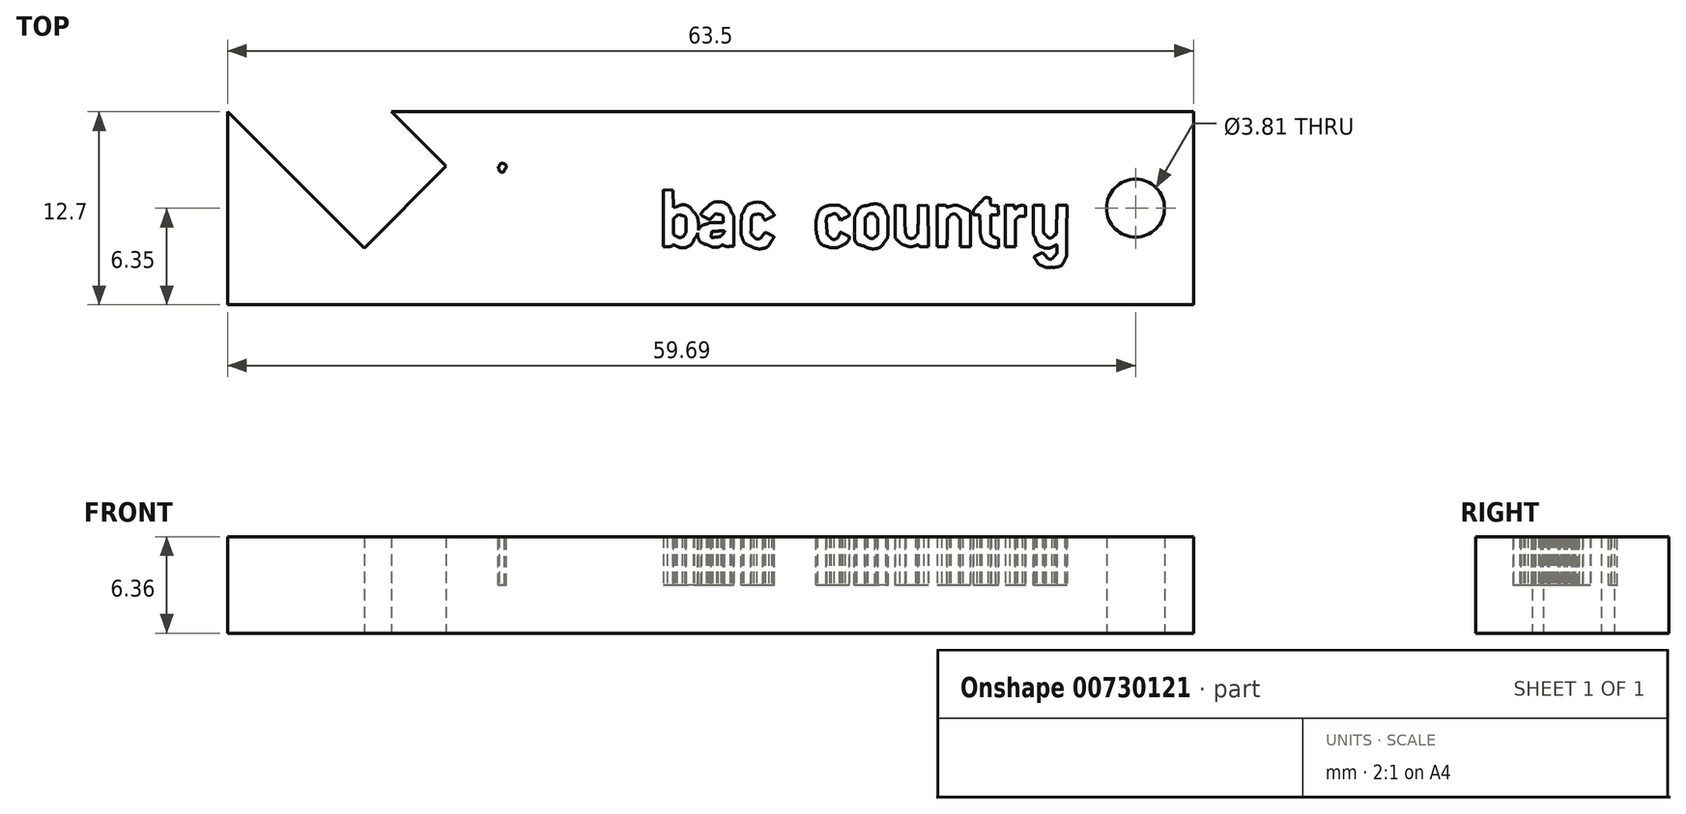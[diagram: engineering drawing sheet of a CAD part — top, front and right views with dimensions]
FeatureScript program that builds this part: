
annotation { "Feature Type Name" : "Feature", "Feature Type Description" : "" }
export const myFeature = defineFeature(function(context is Context, id is Id, definition is map)
    precondition{}
    {
        {
            var Q0;
            Q0=qCreatedBy(makeId("Top.planeOp"),FACE);
            var sketch = newSketch(context, id + "F0", { "sketchPlane" : qUnion([Q0])});
            skLineSegment(sketch, "E0.bottom", {"start": v(31.75, -6.35) * mm, "end": v(-31.75, -6.35) * mm});
            skLineSegment(sketch, "E0.top", {"start": v(31.75, 6.35) * mm, "end": v(-31.75, 6.35) * mm, "construction": true});
            skLineSegment(sketch, "E0.left", {"start": v(31.75, -6.35) * mm, "end": v(31.75, 6.35) * mm});
            skLineSegment(sketch, "E0.right", {"start": v(-31.75, -6.35) * mm, "end": v(-31.75, 6.35) * mm});
            skPoint(sketch, "E0.middle", {"position": v(0, 0) * mm});
            skLineSegment(sketch, "E1", {"start": v(-20.97, 6.35) * mm, "end": v(31.75, 6.35) * mm});
            skLineSegment(sketch, "E2", {"start": v(31.75, 0) * mm, "end": v(27.94, 0) * mm, "construction": true});
            skCircle(sketch, "E3", {"center": v(27.94, 0) * mm, "radius": 1.9 * mm});
            skLineSegment(sketch, "E4", {"start": v(-22.77, -2.63) * mm, "end": v(-17.38, 2.76) * mm});
            skLineSegment(sketch, "E5", {"start": v(-31.75, 6.35) * mm, "end": v(-22.77, -2.63) * mm});
            skLineSegment(sketch, "E6", {"start": v(-20.97, 6.35) * mm, "end": v(-17.38, 2.76) * mm});
            skSolve(sketch);
        }
        {
            var Q0;
            Q0 = qSketchRegion(id + "F0", true);
            extrude(context, id + "F1", {"entities" : qUnion([Q0]), "endBound" : BoundingType.SYMMETRIC, "depth" : 6.35 * mm, "offsetDistance" : 25.4 * mm});
        }
        {
            var Q0;
            Q0=qCreatedBy(makeId("Top.planeOp"),FACE);
            var sketch = newSketch(context, id + "F2", { "sketchPlane" : qUnion([Q0])});
            skFitSpline(sketch, "E7", {"points": [v(-7.2, -5.12) * mm, v(-7.28, -5.08) * mm, v(-7.3, -5) * mm, v(-7.3, -4.6) * mm]});
            skFitSpline(sketch, "E8", {"points": [v(-7.3, -4.6) * mm, v(-7.3, -3.8) * mm, v(-7.5, -3.27) * mm, v(-8, -2.72) * mm]});
            skFitSpline(sketch, "E9", {"points": [v(-8, -2.72) * mm, v(-8.19, -2.52) * mm, v(-8.4, -2.36) * mm, v(-8.62, -2.25) * mm]});
            skFitSpline(sketch, "E10", {"points": [v(-8.62, -2.25) * mm, v(-8.95, -2.1) * mm, v(-8.98, -2.09) * mm, v(-9.6, -2.09) * mm]});
            skFitSpline(sketch, "E11", {"points": [v(-9.6, -2.09) * mm, v(-10.36, -2.09) * mm, v(-10.68, -2.17) * mm, v(-11.16, -2.5) * mm]});
            skFitSpline(sketch, "E12", {"points": [v(-11.16, -2.5) * mm, v(-11.76, -2.9) * mm, v(-12.2, -3.6) * mm, v(-12.44, -4.56) * mm]});
            skFitSpline(sketch, "E13", {"points": [v(-12.97, -5.08) * mm, v(-13.54, -5.08) * mm, v(-13.53, -5.1) * mm, v(-13.39, -4.14) * mm]});
            skFitSpline(sketch, "E14", {"points": [v(-13.39, -4.14) * mm, v(-13.32, -3.71) * mm, v(-13.25, -3.16) * mm, v(-13.23, -2.9) * mm]});
            skLineSegment(sketch, "E15", {"start": v(-12.44, -4.56) * mm, "end": v(-12.58, -5.08) * mm});
            skLineSegment(sketch, "E16", {"start": v(-12.58, -5.08) * mm, "end": v(-12.97, -5.08) * mm});
            skFitSpline(sketch, "E17", {"points": [v(-13.43, -2.09) * mm, v(-13.73, -1.63) * mm, v(-13.83, -1.24) * mm, v(-13.74, -0.83) * mm]});
            skFitSpline(sketch, "E18", {"points": [v(-13.74, -0.83) * mm, v(-13.71, -0.68) * mm, v(-13.56, -0.26) * mm, v(-13.4, 0.1) * mm]});
            skFitSpline(sketch, "E19", {"points": [v(-13.4, 0.1) * mm, v(-13.1, 0.85) * mm, v(-13.05, 1.1) * mm, v(-13.24, 1.23) * mm]});
            skFitSpline(sketch, "E20", {"points": [v(-13.24, 1.23) * mm, v(-13.4, 1.34) * mm, v(-13.55, 1.33) * mm, v(-13.7, 1.22) * mm]});
            skFitSpline(sketch, "E21", {"points": [v(-13.7, 1.22) * mm, v(-13.8, 1.13) * mm, v(-13.82, 1.07) * mm, v(-13.82, 0.8) * mm]});
            skFitSpline(sketch, "E22", {"points": [v(-13.82, 0.8) * mm, v(-13.83, 0.62) * mm, v(-13.83, 0.43) * mm, v(-13.84, 0.38) * mm]});
            skFitSpline(sketch, "E23", {"points": [v(-13.84, 0.38) * mm, v(-13.84, 0.28) * mm, v(-14.07, 0) * mm, v(-14.2, -0.07) * mm]});
            skFitSpline(sketch, "E24", {"points": [v(-14.2, -0.07) * mm, v(-14.3, -0.12) * mm, v(-14.3, -0.12) * mm, v(-14.25, -0.01) * mm]});
            skFitSpline(sketch, "E25", {"points": [v(-14.25, -0.01) * mm, v(-14.15, 0.17) * mm, v(-14.18, 0.5) * mm, v(-14.32, 0.8) * mm]});
            skFitSpline(sketch, "E26", {"points": [v(-14.32, 0.8) * mm, v(-14.4, 0.96) * mm, v(-14.45, 1.14) * mm, v(-14.45, 1.2) * mm]});
            skFitSpline(sketch, "E27", {"points": [v(-14.45, 1.2) * mm, v(-14.46, 1.28) * mm, v(-14.52, 1.38) * mm, v(-14.61, 1.46) * mm]});
            skLineSegment(sketch, "E28", {"start": v(-13.23, -2.9) * mm, "end": v(-13.18, -2.45) * mm});
            skLineSegment(sketch, "E29", {"start": v(-13.18, -2.45) * mm, "end": v(-13.43, -2.09) * mm});
            skFitSpline(sketch, "E30", {"points": [v(-14.69, 1.8) * mm, v(-14.64, 1.91) * mm, v(-14.53, 2.27) * mm, v(-14.45, 2.6) * mm]});
            skFitSpline(sketch, "E31", {"points": [v(-14.45, 2.6) * mm, v(-14.26, 3.33) * mm, v(-14.17, 3.5) * mm, v(-13.8, 3.92) * mm]});
            skFitSpline(sketch, "E32", {"points": [v(-13.8, 3.92) * mm, v(-13.08, 4.73) * mm, v(-12.06, 5.1) * mm, v(-10.83, 5.02) * mm]});
            skFitSpline(sketch, "E33", {"points": [v(-10.83, 5.02) * mm, v(-10.16, 4.98) * mm, v(-9.61, 4.83) * mm, v(-9.01, 4.54) * mm]});
            skFitSpline(sketch, "E34", {"points": [v(-9.01, 4.54) * mm, v(-8.14, 4.1) * mm, v(-7.55, 3.53) * mm, v(-7.15, 2.72) * mm]});
            skFitSpline(sketch, "E35", {"points": [v(-7.15, 2.72) * mm, v(-6.84, 2.1) * mm, v(-6.84, 2) * mm, v(-7.13, 2.36) * mm]});
            skFitSpline(sketch, "E36", {"points": [v(-7.13, 2.36) * mm, v(-7.64, 2.97) * mm, v(-8.27, 3.48) * mm, v(-8.85, 3.74) * mm]});
            skFitSpline(sketch, "E37", {"points": [v(-8.85, 3.74) * mm, v(-9.16, 3.89) * mm, v(-9.86, 4.08) * mm, v(-10.05, 4.07) * mm]});
            skFitSpline(sketch, "E38", {"points": [v(-10.05, 4.07) * mm, v(-10.19, 4.06) * mm, v(-10.18, 4.06) * mm, v(-10.03, 4.01) * mm]});
            skFitSpline(sketch, "E39", {"points": [v(-10.03, 4.01) * mm, v(-8.6, 3.5) * mm, v(-7.65, 2.63) * mm, v(-7.13, 1.31) * mm]});
            skLineSegment(sketch, "E40", {"start": v(-14.61, 1.46) * mm, "end": v(-14.77, 1.6) * mm});
            skLineSegment(sketch, "E41", {"start": v(-14.77, 1.6) * mm, "end": v(-14.69, 1.8) * mm});
            skFitSpline(sketch, "E42", {"points": [v(-7.13, 1.16) * mm, v(-7.62, 1.8) * mm, v(-8.3, 2.37) * mm, v(-8.9, 2.68) * mm]});
            skFitSpline(sketch, "E43", {"points": [v(-8.9, 2.68) * mm, v(-9.76, 3.12) * mm, v(-10.69, 3.14) * mm, v(-11.12, 2.73) * mm]});
            skFitSpline(sketch, "E44", {"points": [v(-11.12, 2.73) * mm, v(-11.63, 2.26) * mm, v(-11.4, 1.47) * mm, v(-10.65, 1.13) * mm]});
            skFitSpline(sketch, "E45", {"points": [v(-10.65, 1.13) * mm, v(-10.24, 0.94) * mm, v(-9.84, 0.86) * mm, v(-8.91, 0.78) * mm]});
            skFitSpline(sketch, "E46", {"points": [v(-8.91, 0.78) * mm, v(-7.92, 0.69) * mm, v(-7.74, 0.65) * mm, v(-7.34, 0.44) * mm]});
            skFitSpline(sketch, "E47", {"points": [v(-7.34, 0.44) * mm, v(-6.83, 0.17) * mm, v(-6.44, -0.3) * mm, v(-6.32, -0.75) * mm]});
            skFitSpline(sketch, "E48", {"points": [v(-6.32, -0.75) * mm, v(-6.25, -1.03) * mm, v(-6.33, -1.46) * mm, v(-6.52, -1.83) * mm]});
            skFitSpline(sketch, "E49", {"points": [v(-6.52, -1.83) * mm, v(-6.76, -2.3) * mm, v(-6.76, -2.56) * mm, v(-6.54, -2.98) * mm]});
            skFitSpline(sketch, "E50", {"points": [v(-6.54, -2.98) * mm, v(-6.46, -3.12) * mm, v(-6.44, -3.32) * mm, v(-6.41, -3.8) * mm]});
            skFitSpline(sketch, "E51", {"points": [v(-6.41, -3.8) * mm, v(-6.4, -4.18) * mm, v(-6.35, -4.56) * mm, v(-6.3, -4.73) * mm]});
            skFitSpline(sketch, "E52", {"points": [v(-6.3, -4.73) * mm, v(-6.18, -5.13) * mm, v(-6.22, -5.18) * mm, v(-6.73, -5.18) * mm]});
            skFitSpline(sketch, "E53", {"points": [v(-6.73, -5.18) * mm, v(-6.94, -5.18) * mm, v(-7.16, -5.15) * mm, v(-7.2, -5.12) * mm]});
            skLineSegment(sketch, "E54", {"start": v(-7.13, 1.31) * mm, "end": v(-7, 0.98) * mm});
            skLineSegment(sketch, "E55", {"start": v(-7, 0.98) * mm, "end": v(-7.13, 1.16) * mm});
            skFitSpline(sketch, "E56", {"points": [v(-13.54, 2.54) * mm, v(-13.41, 2.77) * mm, v(-13.73, 2.97) * mm, v(-13.9, 2.77) * mm]});
            skFitSpline(sketch, "E57", {"points": [v(-13.9, 2.77) * mm, v(-13.94, 2.7) * mm, v(-13.95, 2.66) * mm, v(-13.9, 2.56) * mm]});
            skFitSpline(sketch, "E58", {"points": [v(-13.9, 2.56) * mm, v(-13.83, 2.4) * mm, v(-13.61, 2.4) * mm, v(-13.54, 2.54) * mm]});
            skFitSpline(sketch, "E59", {"points": [v(22, -3.87) * mm, v(21.68, -3.74) * mm, v(21.56, -3.65) * mm, v(21.42, -3.46) * mm]});
            skFitSpline(sketch, "E60", {"points": [v(21.42, -3.46) * mm, v(21.34, -3.34) * mm, v(21.28, -3.22) * mm, v(21.3, -3.2) * mm]});
            skFitSpline(sketch, "E61", {"points": [v(21.3, -3.2) * mm, v(21.3, -3.17) * mm, v(21.44, -3.1) * mm, v(21.58, -3.04) * mm]});
            skLineSegment(sketch, "E62", {"start": v(-13.54, 2.54) * mm, "end": v(-13.54, 2.54) * mm});
            skFitSpline(sketch, "E63", {"points": [v(22, -3.1) * mm, v(22.23, -3.33) * mm, v(22.4, -3.35) * mm, v(22.6, -3.14) * mm]});
            skFitSpline(sketch, "E64", {"points": [v(22.6, -3.14) * mm, v(22.74, -3) * mm, v(22.76, -2.95) * mm, v(22.76, -2.7) * mm]});
            skFitSpline(sketch, "E65", {"points": [v(22.76, -2.7) * mm, v(22.76, -2.44) * mm, v(22.75, -2.41) * mm, v(22.67, -2.44) * mm]});
            skFitSpline(sketch, "E66", {"points": [v(22.67, -2.44) * mm, v(22.2, -2.64) * mm, v(21.57, -2.4) * mm, v(21.34, -1.96) * mm]});
            skFitSpline(sketch, "E67", {"points": [v(21.34, -1.96) * mm, v(21.23, -1.75) * mm, v(21.22, -1.67) * mm, v(21.22, -0.77) * mm]});
            skLineSegment(sketch, "E68", {"start": v(21.58, -3.04) * mm, "end": v(21.83, -2.92) * mm});
            skLineSegment(sketch, "E69", {"start": v(21.83, -2.92) * mm, "end": v(22, -3.1) * mm});
            skFitSpline(sketch, "E70", {"points": [v(22.04, -1.76) * mm, v(22.22, -1.94) * mm, v(22.4, -1.95) * mm, v(22.59, -1.78) * mm]});
            skLineSegment(sketch, "E71", {"start": v(21.22, -0.77) * mm, "end": v(21.22, 0.19) * mm});
            skLineSegment(sketch, "E72", {"start": v(21.22, 0.19) * mm, "end": v(21.56, 0.19) * mm});
            skLineSegment(sketch, "E73", {"start": v(21.56, 0.19) * mm, "end": v(21.89, 0.19) * mm});
            skLineSegment(sketch, "E74", {"start": v(21.89, 0.19) * mm, "end": v(21.89, -0.71) * mm});
            skLineSegment(sketch, "E75", {"start": v(21.89, -0.71) * mm, "end": v(21.89, -1.6) * mm});
            skLineSegment(sketch, "E76", {"start": v(21.89, -1.6) * mm, "end": v(22.04, -1.76) * mm});
            skFitSpline(sketch, "E77", {"points": [v(23.41, -1.49) * mm, v(23.4, -3.07) * mm, v(23.4, -3.17) * mm, v(23.3, -3.36) * mm]});
            skFitSpline(sketch, "E78", {"points": [v(23.3, -3.36) * mm, v(23.12, -3.7) * mm, v(22.84, -3.86) * mm, v(22.42, -3.88) * mm]});
            skFitSpline(sketch, "E79", {"points": [v(22.42, -3.88) * mm, v(22.23, -3.9) * mm, v(22.03, -3.89) * mm, v(22, -3.87) * mm]});
            skLineSegment(sketch, "E80", {"start": v(22.59, -1.78) * mm, "end": v(22.73, -1.66) * mm});
            skLineSegment(sketch, "E81", {"start": v(22.73, -1.66) * mm, "end": v(22.75, -0.74) * mm});
            skLineSegment(sketch, "E82", {"start": v(22.75, -0.74) * mm, "end": v(22.76, 0.19) * mm});
            skLineSegment(sketch, "E83", {"start": v(22.76, 0.19) * mm, "end": v(23.1, 0.19) * mm});
            skLineSegment(sketch, "E84", {"start": v(23.1, 0.19) * mm, "end": v(23.43, 0.19) * mm});
            skLineSegment(sketch, "E85", {"start": v(23.43, 0.19) * mm, "end": v(23.41, -1.49) * mm});
            skFitSpline(sketch, "E86", {"points": [v(2.65, -2.5) * mm, v(2.4, -2.4) * mm, v(2.18, -2.2) * mm, v(2.08, -1.93) * mm]});
            skFitSpline(sketch, "E87", {"points": [v(2.08, -1.93) * mm, v(2.01, -1.77) * mm, v(2, -1.57) * mm, v(2.01, -1.08) * mm]});
            skFitSpline(sketch, "E88", {"points": [v(2.01, -1.08) * mm, v(2.03, -0.49) * mm, v(2.04, -0.43) * mm, v(2.17, -0.24) * mm]});
            skFitSpline(sketch, "E89", {"points": [v(2.17, -0.24) * mm, v(2.5, 0.25) * mm, v(3.38, 0.37) * mm, v(3.82, -0.03) * mm]});
            skFitSpline(sketch, "E90", {"points": [v(3.82, -0.03) * mm, v(3.99, -0.17) * mm, v(4.18, -0.46) * mm, v(4.14, -0.5) * mm]});
            skFitSpline(sketch, "E91", {"points": [v(4.14, -0.5) * mm, v(4.13, -0.5) * mm, v(4, -0.58) * mm, v(3.85, -0.65) * mm]});
            skFitSpline(sketch, "E92", {"points": [v(3.85, -0.65) * mm, v(3.6, -0.78) * mm, v(3.58, -0.79) * mm, v(3.5, -0.7) * mm]});
            skFitSpline(sketch, "E93", {"points": [v(3.5, -0.7) * mm, v(3.47, -0.65) * mm, v(3.44, -0.59) * mm, v(3.44, -0.57) * mm]});
            skFitSpline(sketch, "E94", {"points": [v(3.44, -0.57) * mm, v(3.43, -0.5) * mm, v(3.15, -0.38) * mm, v(3.02, -0.4) * mm]});
            skFitSpline(sketch, "E95", {"points": [v(3.02, -0.4) * mm, v(2.77, -0.46) * mm, v(2.7, -0.6) * mm, v(2.68, -1.07) * mm]});
            skFitSpline(sketch, "E96", {"points": [v(2.68, -1.07) * mm, v(2.66, -1.58) * mm, v(2.68, -1.72) * mm, v(2.83, -1.85) * mm]});
            skFitSpline(sketch, "E97", {"points": [v(2.83, -1.85) * mm, v(3.02, -2.03) * mm, v(3.25, -2) * mm, v(3.43, -1.77) * mm]});
            skLineSegment(sketch, "E98", {"start": v(22, -3.87) * mm, "end": v(22, -3.87) * mm});
            skFitSpline(sketch, "E99", {"points": [v(3.87, -1.72) * mm, v(4.02, -1.8) * mm, v(4.15, -1.88) * mm, v(4.15, -1.9) * mm]});
            skFitSpline(sketch, "E100", {"points": [v(4.15, -1.9) * mm, v(4.15, -1.92) * mm, v(4.08, -2.04) * mm, v(4, -2.15) * mm]});
            skFitSpline(sketch, "E101", {"points": [v(4, -2.15) * mm, v(3.73, -2.53) * mm, v(3.15, -2.68) * mm, v(2.65, -2.5) * mm]});
            skLineSegment(sketch, "E102", {"start": v(3.43, -1.77) * mm, "end": v(3.59, -1.58) * mm});
            skLineSegment(sketch, "E103", {"start": v(3.59, -1.58) * mm, "end": v(3.87, -1.72) * mm});
            skFitSpline(sketch, "E104", {"points": [v(7.63, -2.5) * mm, v(7.37, -2.42) * mm, v(7.1, -2.12) * mm, v(7.02, -1.84) * mm]});
            skFitSpline(sketch, "E105", {"points": [v(7.02, -1.84) * mm, v(6.95, -1.55) * mm, v(6.95, -0.77) * mm, v(7.02, -0.51) * mm]});
            skFitSpline(sketch, "E106", {"points": [v(7.02, -0.51) * mm, v(7.09, -0.27) * mm, v(7.33, 0.02) * mm, v(7.57, 0.12) * mm]});
            skFitSpline(sketch, "E107", {"points": [v(7.57, 0.12) * mm, v(7.68, 0.16) * mm, v(7.9, 0.2) * mm, v(8.1, 0.2) * mm]});
            skFitSpline(sketch, "E108", {"points": [v(8.1, 0.2) * mm, v(8.38, 0.2) * mm, v(8.49, 0.17) * mm, v(8.67, 0.07) * mm]});
            skFitSpline(sketch, "E109", {"points": [v(8.67, 0.07) * mm, v(8.87, -0.05) * mm, v(9.11, -0.34) * mm, v(9.11, -0.46) * mm]});
            skFitSpline(sketch, "E110", {"points": [v(9.11, -0.46) * mm, v(9.11, -0.48) * mm, v(8.98, -0.57) * mm, v(8.83, -0.64) * mm]});
            skFitSpline(sketch, "E111", {"points": [v(8.44, -0.62) * mm, v(8.3, -0.41) * mm, v(8.13, -0.36) * mm, v(7.91, -0.45) * mm]});
            skFitSpline(sketch, "E112", {"points": [v(7.91, -0.45) * mm, v(7.68, -0.54) * mm, v(7.6, -0.77) * mm, v(7.64, -1.3) * mm]});
            skFitSpline(sketch, "E113", {"points": [v(7.64, -1.3) * mm, v(7.66, -1.68) * mm, v(7.68, -1.73) * mm, v(7.8, -1.84) * mm]});
            skFitSpline(sketch, "E114", {"points": [v(7.8, -1.84) * mm, v(8.04, -2.04) * mm, v(8.32, -1.98) * mm, v(8.49, -1.67) * mm]});
            skFitSpline(sketch, "E115", {"points": [v(8.49, -1.67) * mm, v(8.54, -1.58) * mm, v(8.55, -1.58) * mm, v(8.83, -1.72) * mm]});
            skFitSpline(sketch, "E116", {"points": [v(8.83, -1.72) * mm, v(8.98, -1.8) * mm, v(9.11, -1.88) * mm, v(9.11, -1.92) * mm]});
            skFitSpline(sketch, "E117", {"points": [v(9.11, -1.92) * mm, v(9.11, -2.04) * mm, v(8.79, -2.38) * mm, v(8.58, -2.48) * mm]});
            skFitSpline(sketch, "E118", {"points": [v(8.58, -2.48) * mm, v(8.34, -2.58) * mm, v(7.91, -2.6) * mm, v(7.63, -2.5) * mm]});
            skLineSegment(sketch, "E119", {"start": v(8.83, -0.64) * mm, "end": v(8.55, -0.78) * mm});
            skLineSegment(sketch, "E120", {"start": v(8.55, -0.78) * mm, "end": v(8.44, -0.62) * mm});
            skFitSpline(sketch, "E121", {"points": [v(10.11, -2.5) * mm, v(9.63, -2.32) * mm, v(9.47, -2) * mm, v(9.47, -1.19) * mm]});
            skFitSpline(sketch, "E122", {"points": [v(9.47, -1.19) * mm, v(9.47, -0.66) * mm, v(9.48, -0.57) * mm, v(9.6, -0.35) * mm]});
            skFitSpline(sketch, "E123", {"points": [v(9.6, -0.35) * mm, v(9.75, -0.04) * mm, v(9.97, 0.12) * mm, v(10.33, 0.19) * mm]});
            skFitSpline(sketch, "E124", {"points": [v(10.33, 0.19) * mm, v(10.86, 0.29) * mm, v(11.36, 0.07) * mm, v(11.56, -0.35) * mm]});
            skFitSpline(sketch, "E125", {"points": [v(11.56, -0.35) * mm, v(11.67, -0.56) * mm, v(11.67, -0.64) * mm, v(11.66, -1.26) * mm]});
            skFitSpline(sketch, "E126", {"points": [v(11.66, -1.26) * mm, v(11.64, -1.94) * mm, v(11.64, -1.95) * mm, v(11.48, -2.15) * mm]});
            skFitSpline(sketch, "E127", {"points": [v(11.48, -2.15) * mm, v(11.18, -2.53) * mm, v(10.62, -2.68) * mm, v(10.11, -2.5) * mm]});
            skLineSegment(sketch, "E128", {"start": v(7.63, -2.5) * mm, "end": v(7.63, -2.5) * mm});
            skFitSpline(sketch, "E129", {"points": [v(10.8, -1.9) * mm, v(10.96, -1.77) * mm, v(11, -1.6) * mm, v(11, -1.15) * mm]});
            skFitSpline(sketch, "E130", {"points": [v(11, -1.15) * mm, v(11, -0.74) * mm, v(10.99, -0.67) * mm, v(10.88, -0.55) * mm]});
            skFitSpline(sketch, "E131", {"points": [v(10.88, -0.55) * mm, v(10.72, -0.36) * mm, v(10.44, -0.35) * mm, v(10.27, -0.52) * mm]});
            skFitSpline(sketch, "E132", {"points": [v(10.27, -0.52) * mm, v(10.17, -0.62) * mm, v(10.16, -0.68) * mm, v(10.16, -1.17) * mm]});
            skFitSpline(sketch, "E133", {"points": [v(10.16, -1.17) * mm, v(10.16, -1.7) * mm, v(10.16, -1.71) * mm, v(10.3, -1.84) * mm]});
            skFitSpline(sketch, "E134", {"points": [v(10.3, -1.84) * mm, v(10.46, -1.97) * mm, v(10.67, -2) * mm, v(10.8, -1.9) * mm]});
            skFitSpline(sketch, "E135", {"points": [v(18.43, -2.5) * mm, v(18.17, -2.41) * mm, v(17.9, -2.17) * mm, v(17.81, -1.97) * mm]});
            skFitSpline(sketch, "E136", {"points": [v(17.81, -1.97) * mm, v(17.76, -1.84) * mm, v(17.72, -1.55) * mm, v(17.7, -1.1) * mm]});
            skFitSpline(sketch, "E137", {"points": [v(17.49, -0.43) * mm, v(17.3, -0.43) * mm, v(17.29, -0.42) * mm, v(17.29, -0.26) * mm]});
            skFitSpline(sketch, "E138", {"points": [v(17.29, -0.26) * mm, v(17.3, -0.12) * mm, v(17.36, -0.02) * mm, v(17.67, 0.3) * mm]});
            skFitSpline(sketch, "E139", {"points": [v(17.67, 0.3) * mm, v(18, 0.67) * mm, v(18.06, 0.7) * mm, v(18.21, 0.7) * mm]});
            skFitSpline(sketch, "E140", {"points": [v(18.21, 0.7) * mm, v(18.38, 0.67) * mm, v(18.39, 0.67) * mm, v(18.4, 0.43) * mm]});
            skLineSegment(sketch, "E141", {"start": v(17.7, -1.1) * mm, "end": v(17.68, -0.43) * mm});
            skLineSegment(sketch, "E142", {"start": v(17.68, -0.43) * mm, "end": v(17.49, -0.43) * mm});
            skFitSpline(sketch, "E143", {"points": [v(18.41, -1.04) * mm, v(18.41, -1.38) * mm, v(18.44, -1.7) * mm, v(18.46, -1.75) * mm]});
            skFitSpline(sketch, "E144", {"points": [v(18.46, -1.75) * mm, v(18.5, -1.8) * mm, v(18.6, -1.88) * mm, v(18.72, -1.93) * mm]});
            skFitSpline(sketch, "E145", {"points": [v(18.72, -1.93) * mm, v(18.92, -2) * mm, v(18.92, -2) * mm, v(18.92, -2.3) * mm]});
            skLineSegment(sketch, "E146", {"start": v(18.4, 0.43) * mm, "end": v(18.42, 0.2) * mm});
            skLineSegment(sketch, "E147", {"start": v(18.42, 0.2) * mm, "end": v(18.66, 0.18) * mm});
            skLineSegment(sketch, "E148", {"start": v(18.66, 0.18) * mm, "end": v(18.9, 0.16) * mm});
            skLineSegment(sketch, "E149", {"start": v(18.9, 0.16) * mm, "end": v(18.91, -0.13) * mm});
            skLineSegment(sketch, "E150", {"start": v(18.91, -0.13) * mm, "end": v(18.93, -0.43) * mm});
            skLineSegment(sketch, "E151", {"start": v(18.93, -0.43) * mm, "end": v(18.67, -0.43) * mm});
            skLineSegment(sketch, "E152", {"start": v(18.67, -0.43) * mm, "end": v(18.41, -0.43) * mm});
            skLineSegment(sketch, "E153", {"start": v(18.41, -0.43) * mm, "end": v(18.41, -1.04) * mm});
            skFitSpline(sketch, "E154", {"points": [v(18.76, -2.57) * mm, v(18.67, -2.57) * mm, v(18.52, -2.54) * mm, v(18.43, -2.5) * mm]});
            skLineSegment(sketch, "E155", {"start": v(18.92, -2.3) * mm, "end": v(18.92, -2.57) * mm});
            skLineSegment(sketch, "E156", {"start": v(18.92, -2.57) * mm, "end": v(18.76, -2.57) * mm});
            skLineSegment(sketch, "E157", {"start": v(18.43, -2.5) * mm, "end": v(18.43, -2.5) * mm});
            skFitSpline(sketch, "E158", {"points": [v(-2.2, 0.12) * mm, v(-1.83, 0.23) * mm, v(-1.39, 0.08) * mm, v(-1.14, -0.24) * mm]});
            skFitSpline(sketch, "E159", {"points": [v(-1.14, -0.24) * mm, v(-0.87, -0.59) * mm, v(-0.84, -1.6) * mm, v(-1.07, -2.02) * mm]});
            skFitSpline(sketch, "E160", {"points": [v(-1.07, -2.02) * mm, v(-1.28, -2.4) * mm, v(-1.85, -2.6) * mm, v(-2.26, -2.47) * mm]});
            skFitSpline(sketch, "E161", {"points": [v(-2.26, -2.47) * mm, v(-2.4, -2.42) * mm, v(-2.47, -2.42) * mm, v(-2.5, -2.46) * mm]});
            skFitSpline(sketch, "E162", {"points": [v(-2.5, -2.46) * mm, v(-2.54, -2.5) * mm, v(-2.69, -2.52) * mm, v(-2.84, -2.52) * mm]});
            skLineSegment(sketch, "E163", {"start": v(-3.1, -0.65) * mm, "end": v(-3.1, 1.22) * mm});
            skLineSegment(sketch, "E164", {"start": v(-3.1, 1.22) * mm, "end": v(-2.79, 1.2) * mm});
            skLineSegment(sketch, "E165", {"start": v(-2.79, 1.2) * mm, "end": v(-2.47, 1.19) * mm});
            skLineSegment(sketch, "E166", {"start": v(-2.47, 1.19) * mm, "end": v(-2.45, 0.62) * mm});
            skLineSegment(sketch, "E167", {"start": v(-2.45, 0.62) * mm, "end": v(-2.44, 0.05) * mm});
            skLineSegment(sketch, "E168", {"start": v(-2.44, 0.05) * mm, "end": v(-2.2, 0.12) * mm});
            skFitSpline(sketch, "E169", {"points": [v(-1.71, -1.75) * mm, v(-1.64, -1.66) * mm, v(-1.62, -1.54) * mm, v(-1.62, -1.18) * mm]});
            skFitSpline(sketch, "E170", {"points": [v(-1.62, -1.18) * mm, v(-1.62, -0.66) * mm, v(-1.66, -0.56) * mm, v(-1.88, -0.48) * mm]});
            skFitSpline(sketch, "E171", {"points": [v(-1.88, -0.48) * mm, v(-2.06, -0.42) * mm, v(-2.16, -0.45) * mm, v(-2.33, -0.6) * mm]});
            skFitSpline(sketch, "E172", {"points": [v(-2.33, -0.6) * mm, v(-2.43, -0.69) * mm, v(-2.44, -0.75) * mm, v(-2.44, -1.17) * mm]});
            skFitSpline(sketch, "E173", {"points": [v(-2.44, -1.17) * mm, v(-2.44, -1.64) * mm, v(-2.41, -1.74) * mm, v(-2.21, -1.85) * mm]});
            skFitSpline(sketch, "E174", {"points": [v(-2.21, -1.85) * mm, v(-2.07, -1.93) * mm, v(-1.82, -1.88) * mm, v(-1.71, -1.75) * mm]});
            skLineSegment(sketch, "E175", {"start": v(-2.84, -2.52) * mm, "end": v(-3.1, -2.52) * mm});
            skLineSegment(sketch, "E176", {"start": v(-3.1, -2.52) * mm, "end": v(-3.1, -0.65) * mm});
            skFitSpline(sketch, "E177", {"points": [v(-0.2, -2.4) * mm, v(-0.74, -2.12) * mm, v(-0.74, -1.3) * mm, v(-0.2, -1.03) * mm]});
            skFitSpline(sketch, "E178", {"points": [v(-0.2, -1.03) * mm, v(-0.07, -0.96) * mm, v(0.1, -0.94) * mm, v(0.4, -0.94) * mm]});
            skFitSpline(sketch, "E179", {"points": [v(0.83, -0.77) * mm, v(0.83, -0.56) * mm, v(0.71, -0.44) * mm, v(0.48, -0.4) * mm]});
            skFitSpline(sketch, "E180", {"points": [v(0.48, -0.4) * mm, v(0.34, -0.37) * mm, v(0.3, -0.39) * mm, v(0.13, -0.55) * mm]});
            skLineSegment(sketch, "E181", {"start": v(0.4, -0.94) * mm, "end": v(0.83, -0.94) * mm});
            skLineSegment(sketch, "E182", {"start": v(0.83, -0.94) * mm, "end": v(0.83, -0.77) * mm});
            skFitSpline(sketch, "E183", {"points": [v(-0.3, -0.62) * mm, v(-0.45, -0.56) * mm, v(-0.57, -0.49) * mm, v(-0.58, -0.47) * mm]});
            skFitSpline(sketch, "E184", {"points": [v(-0.58, -0.47) * mm, v(-0.63, -0.4) * mm, v(-0.45, -0.13) * mm, v(-0.28, 0) * mm]});
            skFitSpline(sketch, "E185", {"points": [v(-0.28, 0) * mm, v(0.25, 0.4) * mm, v(1.07, 0.27) * mm, v(1.38, -0.27) * mm]});
            skFitSpline(sketch, "E186", {"points": [v(1.38, -0.27) * mm, v(1.52, -0.5) * mm, v(1.52, -0.51) * mm, v(1.52, -1.5) * mm]});
            skLineSegment(sketch, "E187", {"start": v(0.13, -0.55) * mm, "end": v(-0.06, -0.74) * mm});
            skLineSegment(sketch, "E188", {"start": v(-0.06, -0.74) * mm, "end": v(-0.3, -0.62) * mm});
            skFitSpline(sketch, "E189", {"points": [v(1.27, -2.51) * mm, v(1.13, -2.52) * mm, v(0.96, -2.5) * mm, v(0.9, -2.47) * mm]});
            skFitSpline(sketch, "E190", {"points": [v(0.9, -2.47) * mm, v(0.82, -2.42) * mm, v(0.76, -2.42) * mm, v(0.69, -2.46) * mm]});
            skFitSpline(sketch, "E191", {"points": [v(0.69, -2.46) * mm, v(0.5, -2.56) * mm, v(0.05, -2.53) * mm, v(-0.2, -2.4) * mm]});
            skLineSegment(sketch, "E192", {"start": v(1.52, -1.5) * mm, "end": v(1.52, -2.5) * mm});
            skLineSegment(sketch, "E193", {"start": v(1.52, -2.5) * mm, "end": v(1.27, -2.51) * mm});
            skFitSpline(sketch, "E194", {"points": [v(0.74, -1.76) * mm, v(0.91, -1.54) * mm, v(0.86, -1.5) * mm, v(0.46, -1.5) * mm]});
            skFitSpline(sketch, "E195", {"points": [v(0.46, -1.5) * mm, v(0.11, -1.52) * mm, v(0.09, -1.53) * mm, v(0.07, -1.64) * mm]});
            skFitSpline(sketch, "E196", {"points": [v(0.07, -1.64) * mm, v(0.04, -1.88) * mm, v(0.1, -1.92) * mm, v(0.38, -1.9) * mm]});
            skFitSpline(sketch, "E197", {"points": [v(0.38, -1.9) * mm, v(0.57, -1.88) * mm, v(0.67, -1.84) * mm, v(0.74, -1.76) * mm]});
            skLineSegment(sketch, "E198", {"start": v(-0.2, -2.4) * mm, "end": v(-0.2, -2.4) * mm});
            skFitSpline(sketch, "E199", {"points": [v(5.17, 0.34) * mm, v(5.17, -0.22) * mm, v(5.2, -0.48) * mm, v(5.23, -0.5) * mm]});
            skFitSpline(sketch, "E200", {"points": [v(5.23, -0.5) * mm, v(5.27, -0.53) * mm, v(5.42, -0.4) * mm, v(5.63, -0.18) * mm]});
            skLineSegment(sketch, "E201", {"start": v(4.5, -0.68) * mm, "end": v(4.5, 1.16) * mm});
            skLineSegment(sketch, "E202", {"start": v(4.5, 1.16) * mm, "end": v(4.84, 1.16) * mm});
            skLineSegment(sketch, "E203", {"start": v(4.84, 1.16) * mm, "end": v(5.17, 1.16) * mm});
            skLineSegment(sketch, "E204", {"start": v(5.17, 1.16) * mm, "end": v(5.17, 0.34) * mm});
            skFitSpline(sketch, "E205", {"points": [v(6.34, 0.19) * mm, v(6.6, 0.19) * mm, v(6.7, 0.17) * mm, v(6.7, 0.12) * mm]});
            skFitSpline(sketch, "E206", {"points": [v(6.7, 0.12) * mm, v(6.7, 0.09) * mm, v(6.52, -0.12) * mm, v(6.3, -0.35) * mm]});
            skFitSpline(sketch, "E207", {"points": [v(6.3, -0.35) * mm, v(6.07, -0.57) * mm, v(5.89, -0.77) * mm, v(5.89, -0.8) * mm]});
            skFitSpline(sketch, "E208", {"points": [v(5.89, -0.8) * mm, v(5.89, -0.82) * mm, v(6.1, -1.16) * mm, v(6.34, -1.56) * mm]});
            skFitSpline(sketch, "E209", {"points": [v(6.34, -1.56) * mm, v(7, -2.64) * mm, v(6.99, -2.52) * mm, v(6.5, -2.52) * mm]});
            skLineSegment(sketch, "E210", {"start": v(5.63, -0.18) * mm, "end": v(5.97, 0.2) * mm});
            skLineSegment(sketch, "E211", {"start": v(5.97, 0.2) * mm, "end": v(6.34, 0.19) * mm});
            skFitSpline(sketch, "E212", {"points": [v(5.86, -2.12) * mm, v(5.31, -1.24) * mm, v(5.38, -1.32) * mm, v(5.27, -1.42) * mm]});
            skFitSpline(sketch, "E213", {"points": [v(5.27, -1.42) * mm, v(5.19, -1.5) * mm, v(5.17, -1.59) * mm, v(5.17, -2.02) * mm]});
            skLineSegment(sketch, "E214", {"start": v(6.5, -2.52) * mm, "end": v(6.1, -2.52) * mm});
            skLineSegment(sketch, "E215", {"start": v(6.1, -2.52) * mm, "end": v(5.86, -2.12) * mm});
            skFitSpline(sketch, "E216", {"points": [v(12.8, -2.44) * mm, v(12.67, -2.4) * mm, v(12.5, -2.31) * mm, v(12.43, -2.24) * mm]});
            skFitSpline(sketch, "E217", {"points": [v(12.43, -2.24) * mm, v(12.15, -1.97) * mm, v(12.13, -1.85) * mm, v(12.13, -0.79) * mm]});
            skLineSegment(sketch, "E218", {"start": v(5.17, -2.02) * mm, "end": v(5.17, -2.52) * mm});
            skLineSegment(sketch, "E219", {"start": v(5.17, -2.52) * mm, "end": v(4.84, -2.52) * mm});
            skLineSegment(sketch, "E220", {"start": v(4.84, -2.52) * mm, "end": v(4.5, -2.52) * mm});
            skLineSegment(sketch, "E221", {"start": v(4.5, -2.52) * mm, "end": v(4.5, -0.68) * mm});
            skFitSpline(sketch, "E222", {"points": [v(12.78, -0.7) * mm, v(12.79, -1.23) * mm, v(12.81, -1.62) * mm, v(12.85, -1.69) * mm]});
            skFitSpline(sketch, "E223", {"points": [v(12.85, -1.69) * mm, v(12.97, -1.93) * mm, v(13.35, -1.96) * mm, v(13.54, -1.74) * mm]});
            skFitSpline(sketch, "E224", {"points": [v(13.54, -1.74) * mm, v(13.62, -1.65) * mm, v(13.64, -1.53) * mm, v(13.65, -0.72) * mm]});
            skLineSegment(sketch, "E225", {"start": v(12.13, -0.79) * mm, "end": v(12.13, 0.2) * mm});
            skLineSegment(sketch, "E226", {"start": v(12.13, 0.2) * mm, "end": v(12.45, 0.18) * mm});
            skLineSegment(sketch, "E227", {"start": v(12.45, 0.18) * mm, "end": v(12.76, 0.16) * mm});
            skLineSegment(sketch, "E228", {"start": v(12.76, 0.16) * mm, "end": v(12.78, -0.7) * mm});
            skFitSpline(sketch, "E229", {"points": [v(14.02, -2.52) * mm, v(13.83, -2.52) * mm, v(13.71, -2.5) * mm, v(13.7, -2.46) * mm]});
            skFitSpline(sketch, "E230", {"points": [v(13.7, -2.46) * mm, v(13.68, -2.41) * mm, v(13.63, -2.41) * mm, v(13.47, -2.46) * mm]});
            skFitSpline(sketch, "E231", {"points": [v(13.47, -2.46) * mm, v(13.21, -2.54) * mm, v(13.08, -2.53) * mm, v(12.8, -2.44) * mm]});
            skLineSegment(sketch, "E232", {"start": v(13.65, -0.72) * mm, "end": v(13.67, 0.2) * mm});
            skLineSegment(sketch, "E233", {"start": v(13.67, 0.2) * mm, "end": v(13.98, 0.18) * mm});
            skLineSegment(sketch, "E234", {"start": v(13.98, 0.18) * mm, "end": v(14.3, 0.16) * mm});
            skLineSegment(sketch, "E235", {"start": v(14.3, 0.16) * mm, "end": v(14.31, -1.18) * mm});
            skLineSegment(sketch, "E236", {"start": v(14.31, -1.18) * mm, "end": v(14.33, -2.52) * mm});
            skLineSegment(sketch, "E237", {"start": v(14.33, -2.52) * mm, "end": v(14.02, -2.52) * mm});
            skLineSegment(sketch, "E238", {"start": v(12.8, -2.44) * mm, "end": v(12.8, -2.44) * mm});
            skFitSpline(sketch, "E239", {"points": [v(15.19, 0.19) * mm, v(15.37, 0.19) * mm, v(15.5, 0.17) * mm, v(15.51, 0.13) * mm]});
            skFitSpline(sketch, "E240", {"points": [v(15.51, 0.13) * mm, v(15.53, 0.08) * mm, v(15.59, 0.08) * mm, v(15.77, 0.13) * mm]});
            skFitSpline(sketch, "E241", {"points": [v(15.77, 0.13) * mm, v(16.05, 0.2) * mm, v(16.3, 0.17) * mm, v(16.57, 0.03) * mm]});
            skFitSpline(sketch, "E242", {"points": [v(16.57, 0.03) * mm, v(17.02, -0.2) * mm, v(17.08, -0.4) * mm, v(17.08, -1.57) * mm]});
            skLineSegment(sketch, "E243", {"start": v(14.89, -1.17) * mm, "end": v(14.89, 0.19) * mm});
            skLineSegment(sketch, "E244", {"start": v(14.89, 0.19) * mm, "end": v(15.19, 0.19) * mm});
            skFitSpline(sketch, "E245", {"points": [v(16.42, -1.63) * mm, v(16.42, -0.76) * mm, v(16.42, -0.73) * mm, v(16.3, -0.6) * mm]});
            skFitSpline(sketch, "E246", {"points": [v(16.3, -0.6) * mm, v(16.14, -0.41) * mm, v(15.86, -0.4) * mm, v(15.7, -0.57) * mm]});
            skFitSpline(sketch, "E247", {"points": [v(15.7, -0.57) * mm, v(15.58, -0.68) * mm, v(15.58, -0.73) * mm, v(15.56, -1.6) * mm]});
            skLineSegment(sketch, "E248", {"start": v(17.08, -1.57) * mm, "end": v(17.08, -2.52) * mm});
            skLineSegment(sketch, "E249", {"start": v(17.08, -2.52) * mm, "end": v(16.75, -2.52) * mm});
            skLineSegment(sketch, "E250", {"start": v(16.75, -2.52) * mm, "end": v(16.42, -2.52) * mm});
            skLineSegment(sketch, "E251", {"start": v(16.42, -2.52) * mm, "end": v(16.42, -1.63) * mm});
            skLineSegment(sketch, "E252", {"start": v(15.56, -1.6) * mm, "end": v(15.54, -2.52) * mm});
            skLineSegment(sketch, "E253", {"start": v(15.54, -2.52) * mm, "end": v(15.22, -2.52) * mm});
            skLineSegment(sketch, "E254", {"start": v(15.22, -2.52) * mm, "end": v(14.89, -2.52) * mm});
            skLineSegment(sketch, "E255", {"start": v(14.89, -2.52) * mm, "end": v(14.89, -1.17) * mm});
            skFitSpline(sketch, "E256", {"points": [v(19.67, 0.19) * mm, v(19.91, 0.19) * mm, v(19.96, 0.17) * mm, v(19.98, 0.09) * mm]});
            skFitSpline(sketch, "E257", {"points": [v(19.98, 0.09) * mm, v(20.01, -0.02) * mm, v(20.08, -0.05) * mm, v(20.12, 0.03) * mm]});
            skFitSpline(sketch, "E258", {"points": [v(20.12, 0.03) * mm, v(20.17, 0.1) * mm, v(20.53, 0.2) * mm, v(20.63, 0.16) * mm]});
            skFitSpline(sketch, "E259", {"points": [v(20.63, 0.16) * mm, v(20.7, 0.13) * mm, v(20.71, 0.05) * mm, v(20.71, -0.2) * mm]});
            skLineSegment(sketch, "E260", {"start": v(19.38, -1.17) * mm, "end": v(19.38, 0.19) * mm});
            skLineSegment(sketch, "E261", {"start": v(19.38, 0.19) * mm, "end": v(19.67, 0.19) * mm});
            skFitSpline(sketch, "E262", {"points": [v(20.5, -0.53) * mm, v(20.33, -0.53) * mm, v(20.24, -0.56) * mm, v(20.16, -0.65) * mm]});
            skFitSpline(sketch, "E263", {"points": [v(20.16, -0.65) * mm, v(20.05, -0.76) * mm, v(20.05, -0.81) * mm, v(20.05, -1.64) * mm]});
            skLineSegment(sketch, "E264", {"start": v(20.71, -0.2) * mm, "end": v(20.71, -0.53) * mm});
            skLineSegment(sketch, "E265", {"start": v(20.71, -0.53) * mm, "end": v(20.5, -0.53) * mm});
            skLineSegment(sketch, "E266", {"start": v(20.05, -1.64) * mm, "end": v(20.05, -2.52) * mm});
            skLineSegment(sketch, "E267", {"start": v(20.05, -2.52) * mm, "end": v(19.72, -2.52) * mm});
            skLineSegment(sketch, "E268", {"start": v(19.72, -2.52) * mm, "end": v(19.38, -2.52) * mm});
            skLineSegment(sketch, "E269", {"start": v(19.38, -2.52) * mm, "end": v(19.38, -1.17) * mm});
            skLineSegment(sketch, "E270", {"start": v(-13.33, 5.06) * mm, "end": v(-6.23, 5.06) * mm, "construction": true});
            skSolve(sketch);
        }
        {
            var Q0;
            Q0 = qSketchRegion(id + "F2", true);
            var Q1;
            Q1=makeQuery(id+"F1.opExtrude","CAP_FACE",FACE,{"disambiguationData":[OSD([sQuery(id+"F0.wireOp",EDGE,"E0.bottom"),sQuery(id+"F0.wireOp",EDGE,"E0.left"),sQuery(id+"F0.wireOp",EDGE,"E0.right"),sQuery(id+"F0.wireOp",EDGE,"E1"),sQuery(id+"F0.wireOp",EDGE,"E3"),sQuery(id+"F0.wireOp",EDGE,"E4"),sQuery(id+"F0.wireOp",EDGE,"E5"),sQuery(id+"F0.wireOp",EDGE,"E6")])],"isStart":false});
            extrude(context, id + "F3", {"entities" : qUnion([Q0]), "operationType" : NewBodyOperationType.REMOVE, "depth" : 25.4 * mm, "endBoundEntityFace" : qUnion([Q1]), "hasOffset" : true, "offsetDistance" : 1.27 * mm});
        }
    });
